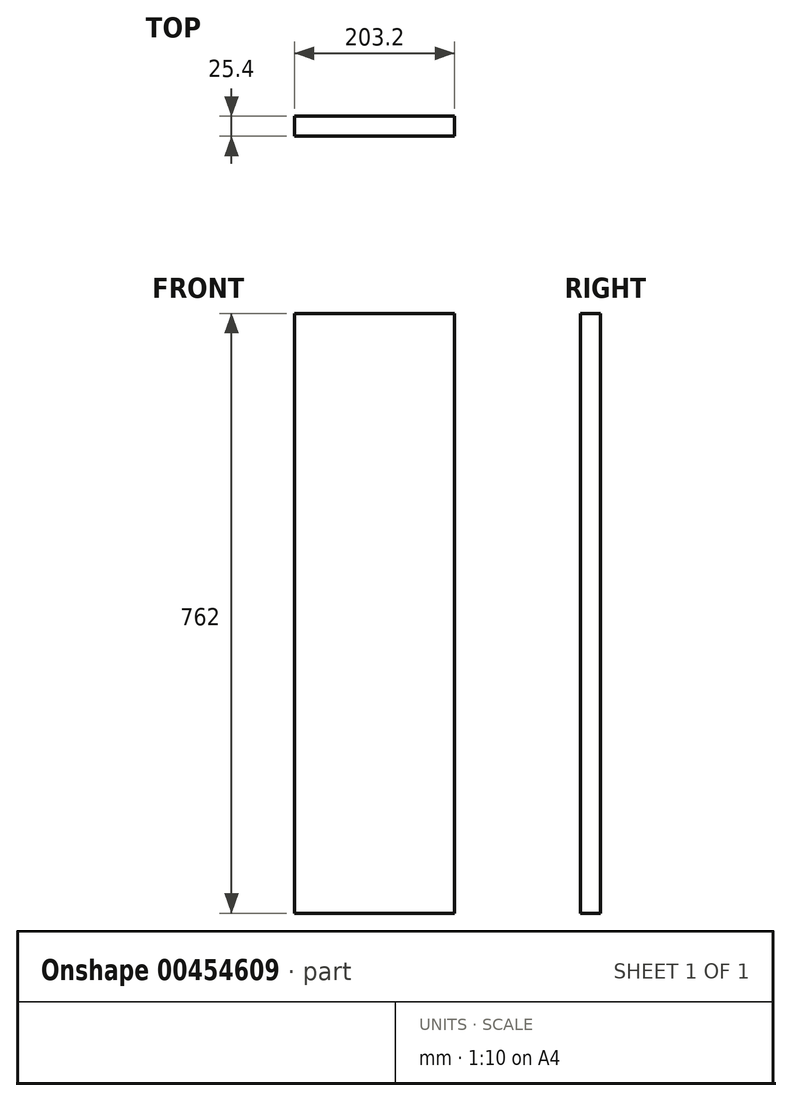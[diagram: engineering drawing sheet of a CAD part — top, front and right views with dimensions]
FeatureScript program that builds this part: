
annotation { "Feature Type Name" : "Feature", "Feature Type Description" : "" }
export const myFeature = defineFeature(function(context is Context, id is Id, definition is map)
    precondition{}
    {
        {
            var Q0;
            Q0=qCreatedBy(makeId("Top.planeOp"),FACE);
            var sketch = newSketch(context, id + "F0", { "sketchPlane" : qUnion([Q0])});
            skLineSegment(sketch, "E0.bottom", {"start": v(101.6, 12.7) * mm, "end": v(-101.6, 12.7) * mm});
            skLineSegment(sketch, "E0.top", {"start": v(101.6, -12.7) * mm, "end": v(-101.6, -12.7) * mm});
            skLineSegment(sketch, "E0.left", {"start": v(101.6, 12.7) * mm, "end": v(101.6, -12.7) * mm});
            skLineSegment(sketch, "E0.right", {"start": v(-101.6, 12.7) * mm, "end": v(-101.6, -12.7) * mm});
            skPoint(sketch, "E0.middle", {"position": v(0, 0) * mm});
            skSolve(sketch);
        }
        {
            var Q0;
            Q0=makeQuery(id+"F0.imprint","IMPRINT",FACE,{"disambiguationData":[TD([[makeQuery(id+"F0.imprint","IMPRINT",EDGE,{"derivedFrom":sQuery(id+"F0.wireOp",EDGE,"E0.bottom")}),1.0]])]});
            extrude(context, id + "F1", {"entities" : qUnion([Q0]), "depth" : 762 * mm});
        }
    });
